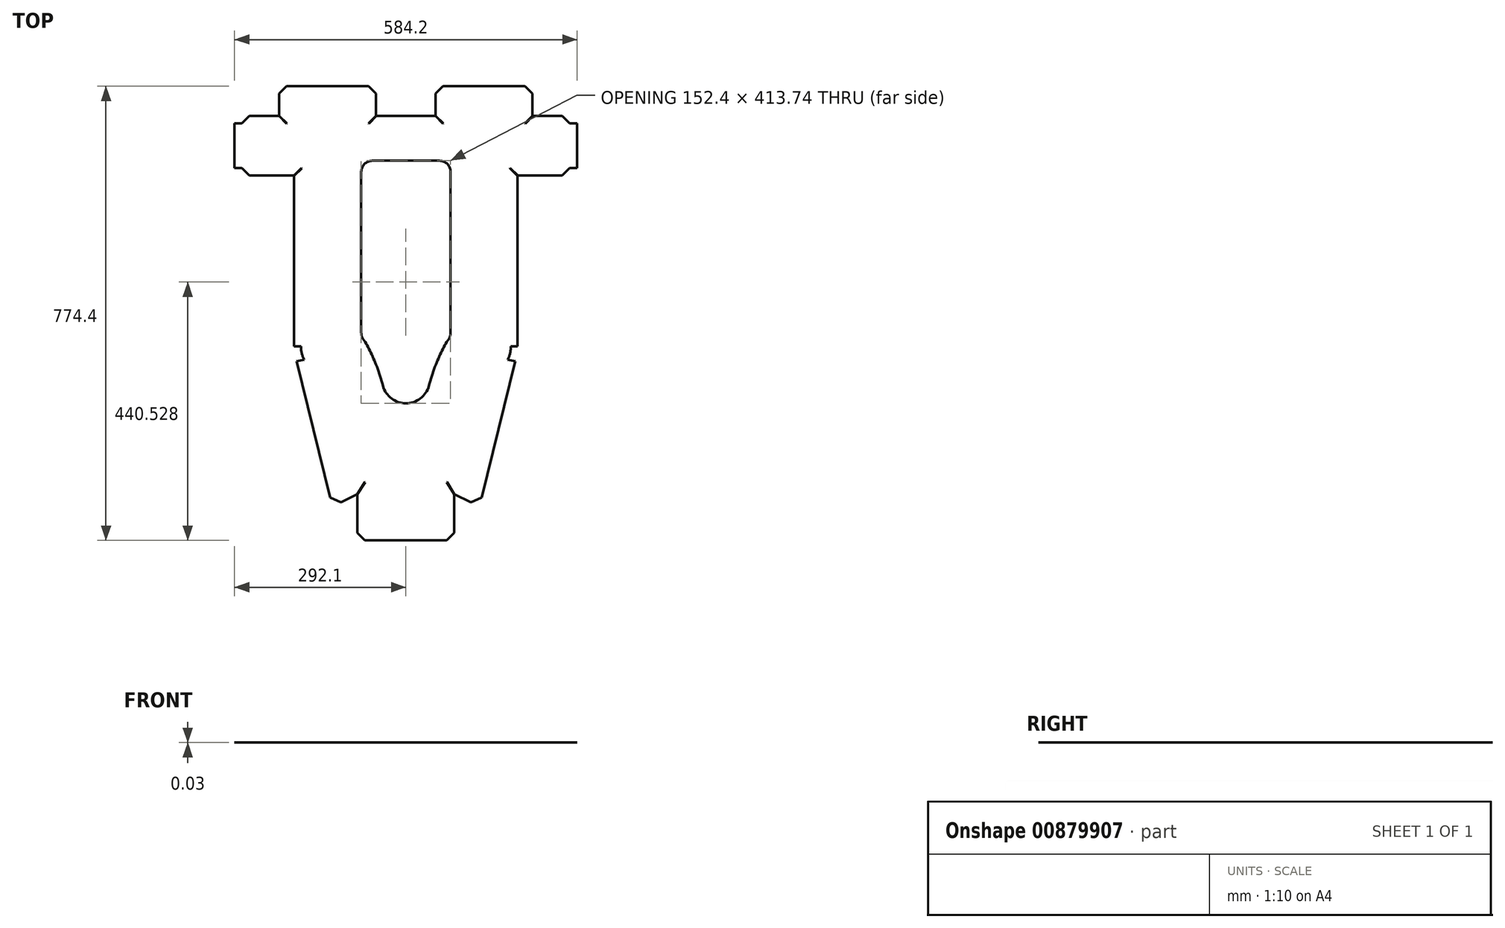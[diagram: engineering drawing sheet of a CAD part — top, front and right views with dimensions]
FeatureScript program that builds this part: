
annotation { "Feature Type Name" : "Feature", "Feature Type Description" : "" }
export const myFeature = defineFeature(function(context is Context, id is Id, definition is map)
    precondition{}
    {
        {
            var Q0;
            Q0=qCreatedBy(makeId("Top.planeOp"),FACE);
            var sketch = newSketch(context, id + "F0", { "sketchPlane" : qUnion([Q0])});
            skLineSegment(sketch, "E0", {"start": v(-107.95, 650.14) * mm, "end": v(-95.25, 650.14) * mm, "construction": true});
            skLineSegment(sketch, "E1", {"start": v(-76.2, 631.09) * mm, "end": v(-76.2, 599.34) * mm, "construction": true});
            skLineSegment(sketch, "E2", {"start": v(-76.2, 599.34) * mm, "end": v(0, 599.34) * mm, "construction": true});
            skLineSegment(sketch, "E3", {"start": v(-127, 631.09) * mm, "end": v(-127, 245.3) * mm, "construction": true});
            skPoint(sketch, "E4", {"position": v(-127, 232) * mm});
            skLineSegment(sketch, "E5", {"start": v(0, 599.34) * mm, "end": v(0, 0) * mm, "construction": true});
            skLineSegment(sketch, "E6", {"start": v(0, 0) * mm, "end": v(-69.85, 0) * mm, "construction": true});
            skLineSegment(sketch, "E7", {"start": v(-69.85, 0) * mm, "end": v(-69.85, -22.66) * mm, "construction": true});
            skLineSegment(sketch, "E8", {"start": v(-69.85, -22.66) * mm, "end": v(0, -22.66) * mm, "construction": true});
            skPoint(sketch, "E9.visualSharp", {"position": v(-127, 650.14) * mm});
            skArc(sketch, "E9.filletArc", {"start": v(-107.95, 650.14) * mm, "mid": v(-121.42, 644.56) * mm, "end": v(-127, 631.09) * mm, "construction": true});
            skPoint(sketch, "E10.visualSharp", {"position": v(-76.2, 650.14) * mm});
            skArc(sketch, "E10.filletArc", {"start": v(-76.2, 631.09) * mm, "mid": v(-81.78, 644.56) * mm, "end": v(-95.25, 650.14) * mm, "construction": true});
            skLineSegment(sketch, "E11", {"start": v(-190.5, 523.14) * mm, "end": v(-190.5, 232) * mm});
            skLineSegment(sketch, "E12", {"start": v(0, 624.74) * mm, "end": v(-50.8, 624.74) * mm});
            skLineSegment(sketch, "E13", {"start": v(-127, 232) * mm, "end": v(-69.85, 0) * mm, "construction": true});
            skLineSegment(sketch, "E14", {"start": v(-127, 232) * mm, "end": v(-185.44, 203.74) * mm, "construction": true});
            skLineSegment(sketch, "E15", {"start": v(-185.44, 203.74) * mm, "end": v(-128.93, -25.64) * mm});
            skLineSegment(sketch, "E16", {"start": v(-127, 232) * mm, "end": v(0, 232) * mm, "construction": true});
            skLineSegment(sketch, "E17", {"start": v(-127, 232) * mm, "end": v(-190.5, 232) * mm, "construction": true});
            skPoint(sketch, "E18.endSnap0", {"position": v(-177.62, 220.4) * mm});
            skLineSegment(sketch, "E19", {"start": v(-177.62, 220.4) * mm, "end": v(-127, 232) * mm, "construction": true});
            skLineSegment(sketch, "E20", {"start": v(-82.55, -86.16) * mm, "end": v(-82.55, -20.25) * mm});
            skLineSegment(sketch, "E21", {"start": v(-82.55, -20.25) * mm, "end": v(-69.85, 0) * mm, "construction": true});
            skLineSegment(sketch, "E22", {"start": v(-82.55, -86.16) * mm, "end": v(-69.85, -86.16) * mm, "construction": true});
            skLineSegment(sketch, "E23", {"start": v(-69.85, -86.16) * mm, "end": v(-69.85, -98.86) * mm, "construction": true});
            skLineSegment(sketch, "E24", {"start": v(-69.85, -98.86) * mm, "end": v(0, -98.86) * mm});
            skLineSegment(sketch, "E25", {"start": v(-111.07, -34.04) * mm, "end": v(-82.55, -20.25) * mm});
            skLineSegment(sketch, "E26", {"start": v(-69.85, -98.86) * mm, "end": v(-82.55, -86.16) * mm});
            skPoint(sketch, "E27.orphan", {"position": v(-127, 599.34) * mm});
            skLineSegment(sketch, "E28.MirrorCS", {"start": v(190.5, 523.14) * mm, "end": v(190.5, 232) * mm});
            skLineSegment(sketch, "E29.MirrorCS", {"start": v(185.44, 203.74) * mm, "end": v(128.93, -25.64) * mm});
            skLineSegment(sketch, "E30.MirrorCS", {"start": v(111.07, -34.04) * mm, "end": v(82.55, -20.25) * mm});
            skLineSegment(sketch, "E31.MirrorCS", {"start": v(82.55, -86.16) * mm, "end": v(82.55, -20.25) * mm});
            skLineSegment(sketch, "E32.MirrorCS", {"start": v(69.85, -98.86) * mm, "end": v(82.55, -86.16) * mm});
            skLineSegment(sketch, "E33.MirrorCS", {"start": v(69.85, -98.86) * mm, "end": v(0, -98.86) * mm});
            skLineSegment(sketch, "E34.MirrorCS", {"start": v(82.55, -20.25) * mm, "end": v(69.85, 0) * mm, "construction": true});
            skArc(sketch, "E35", {"start": v(-178.93, 232) * mm, "mid": v(-177.62, 220.4) * mm, "end": v(-173.75, 209.4) * mm});
            skLineSegment(sketch, "E36", {"start": v(-178.93, 232) * mm, "end": v(-190.5, 232) * mm});
            skLineSegment(sketch, "E37", {"start": v(-173.75, 209.4) * mm, "end": v(-186.08, 206.36) * mm});
            skLineSegment(sketch, "E38", {"start": v(-186.08, 206.36) * mm, "end": v(-185.44, 203.74) * mm});
            skArc(sketch, "E39.MirrorCS", {"start": v(178.93, 232) * mm, "mid": v(177.62, 220.4) * mm, "end": v(173.75, 209.4) * mm});
            skLineSegment(sketch, "E40.MirrorCS", {"start": v(178.93, 232) * mm, "end": v(190.5, 232) * mm});
            skLineSegment(sketch, "E41", {"start": v(-128.93, -25.64) * mm, "end": v(-116.6, -22.6) * mm, "construction": true});
            skLineSegment(sketch, "E42", {"start": v(-116.6, -22.6) * mm, "end": v(-111.07, -34.04) * mm, "construction": true});
            skLineSegment(sketch, "E43", {"start": v(-69.85, 0) * mm, "end": v(-116.6, -22.6) * mm, "construction": true});
            skLineSegment(sketch, "E44.MirrorCS", {"start": v(173.75, 209.4) * mm, "end": v(186.08, 206.36) * mm});
            skLineSegment(sketch, "E45.MirrorCS", {"start": v(186.08, 206.36) * mm, "end": v(185.44, 203.74) * mm});
            skLineSegment(sketch, "E46", {"start": v(-128.93, -25.64) * mm, "end": v(-111.07, -34.04) * mm});
            skLineSegment(sketch, "E47.MirrorCS", {"start": v(128.93, -25.64) * mm, "end": v(111.07, -34.04) * mm});
            skLineSegment(sketch, "E48", {"start": v(-190.5, 523.14) * mm, "end": v(-177.8, 535.84) * mm, "construction": true});
            skLineSegment(sketch, "E49", {"start": v(-190.5, 523.14) * mm, "end": v(-266.7, 523.14) * mm});
            skLineSegment(sketch, "E50", {"start": v(-266.7, 523.14) * mm, "end": v(-266.7, 535.84) * mm, "construction": true});
            skLineSegment(sketch, "E51", {"start": v(-279.4, 535.84) * mm, "end": v(-292.1, 535.84) * mm});
            skLineSegment(sketch, "E52", {"start": v(-292.1, 535.84) * mm, "end": v(-292.1, 612.04) * mm});
            skLineSegment(sketch, "E53", {"start": v(-50.8, 624.74) * mm, "end": v(-50.8, 662.84) * mm});
            skLineSegment(sketch, "E54", {"start": v(-50.8, 624.74) * mm, "end": v(-63.5, 612.04) * mm, "construction": true});
            skLineSegment(sketch, "E55", {"start": v(-63.5, 612.04) * mm, "end": v(-76.2, 612.04) * mm, "construction": true});
            skLineSegment(sketch, "E56", {"start": v(-63.5, 612.04) * mm, "end": v(-63.5, 599.34) * mm, "construction": true});
            skLineSegment(sketch, "E57", {"start": v(-292.1, 612.04) * mm, "end": v(-279.4, 612.04) * mm});
            skLineSegment(sketch, "E58", {"start": v(-266.7, 612.04) * mm, "end": v(-266.7, 624.74) * mm, "construction": true});
            skLineSegment(sketch, "E59", {"start": v(-127, 675.54) * mm, "end": v(-63.5, 675.54) * mm});
            skPoint(sketch, "E60", {"position": v(-63.5, 662.84) * mm});
            skLineSegment(sketch, "E61", {"start": v(-279.4, 535.84) * mm, "end": v(-266.7, 523.14) * mm});
            skLineSegment(sketch, "E62", {"start": v(-279.4, 612.04) * mm, "end": v(-266.7, 624.74) * mm});
            skLineSegment(sketch, "E63", {"start": v(-266.7, 612.04) * mm, "end": v(-279.4, 612.04) * mm, "construction": true});
            skLineSegment(sketch, "E64", {"start": v(-279.4, 535.84) * mm, "end": v(-266.7, 535.84) * mm, "construction": true});
            skLineSegment(sketch, "E65", {"start": v(-127, 675.54) * mm, "end": v(-203.2, 675.54) * mm});
            skLineSegment(sketch, "E66", {"start": v(-215.9, 662.84) * mm, "end": v(-215.9, 624.74) * mm});
            skLineSegment(sketch, "E67", {"start": v(-266.7, 624.74) * mm, "end": v(-215.9, 624.74) * mm});
            skLineSegment(sketch, "E68", {"start": v(-215.9, 624.74) * mm, "end": v(-203.2, 612.04) * mm, "construction": true});
            skLineSegment(sketch, "E69.MirrorCS", {"start": v(190.5, 523.14) * mm, "end": v(177.8, 535.84) * mm, "construction": true});
            skLineSegment(sketch, "E70.MirrorCS", {"start": v(190.5, 523.14) * mm, "end": v(266.7, 523.14) * mm});
            skLineSegment(sketch, "E71.MirrorCS", {"start": v(279.4, 535.84) * mm, "end": v(266.7, 523.14) * mm});
            skLineSegment(sketch, "E72.MirrorCS", {"start": v(279.4, 535.84) * mm, "end": v(292.1, 535.84) * mm});
            skLineSegment(sketch, "E73.MirrorCS", {"start": v(292.1, 535.84) * mm, "end": v(292.1, 612.04) * mm});
            skLineSegment(sketch, "E74.MirrorCS", {"start": v(292.1, 612.04) * mm, "end": v(279.4, 612.04) * mm});
            skLineSegment(sketch, "E75.MirrorCS", {"start": v(279.4, 612.04) * mm, "end": v(266.7, 624.74) * mm});
            skLineSegment(sketch, "E76.MirrorCS", {"start": v(266.7, 624.74) * mm, "end": v(215.9, 624.74) * mm});
            skLineSegment(sketch, "E77.MirrorCS", {"start": v(215.9, 624.74) * mm, "end": v(203.2, 612.04) * mm, "construction": true});
            skLineSegment(sketch, "E78.MirrorCS", {"start": v(50.8, 624.74) * mm, "end": v(63.5, 612.04) * mm, "construction": true});
            skLineSegment(sketch, "E79.MirrorCS", {"start": v(0, 624.74) * mm, "end": v(50.8, 624.74) * mm});
            skLineSegment(sketch, "E80", {"start": v(-215.9, 662.84) * mm, "end": v(-203.2, 675.54) * mm});
            skPoint(sketch, "E81", {"position": v(-63.5, 675.54) * mm});
            skPoint(sketch, "E82", {"position": v(-50.8, 662.84) * mm});
            skLineSegment(sketch, "E83", {"start": v(-63.5, 675.54) * mm, "end": v(-50.8, 662.84) * mm});
            skLineSegment(sketch, "E84.MirrorCS", {"start": v(215.9, 662.84) * mm, "end": v(215.9, 624.74) * mm});
            skLineSegment(sketch, "E85.MirrorCS", {"start": v(215.9, 662.84) * mm, "end": v(203.2, 675.54) * mm});
            skLineSegment(sketch, "E86.MirrorCS", {"start": v(127, 675.54) * mm, "end": v(203.2, 675.54) * mm});
            skLineSegment(sketch, "E87.MirrorCS", {"start": v(127, 675.54) * mm, "end": v(63.5, 675.54) * mm});
            skLineSegment(sketch, "E88.MirrorCS", {"start": v(63.5, 675.54) * mm, "end": v(50.8, 662.84) * mm});
            skLineSegment(sketch, "E89.MirrorCS", {"start": v(50.8, 624.74) * mm, "end": v(50.8, 662.84) * mm});
            skLineSegment(sketch, "E90", {"start": v(0, 548.54) * mm, "end": v(-57.15, 548.54) * mm, "construction": true});
            skPoint(sketch, "E91", {"position": v(0, 134.8) * mm});
            skArc(sketch, "E92", {"start": v(0, 134.8) * mm, "mid": v(-24.7, 143.14) * mm, "end": v(-39.26, 164.76) * mm});
            skArc(sketch, "E93", {"start": v(0, 548.54) * mm, "mid": v(-53.88, 526.22) * mm, "end": v(-76.2, 472.34) * mm, "construction": true});
            skLineSegment(sketch, "E94", {"start": v(-76.2, 472.34) * mm, "end": v(-76.2, 255.45) * mm});
            skLineSegment(sketch, "E95", {"start": v(-76.2, 529.49) * mm, "end": v(-76.2, 472.34) * mm});
            skPoint(sketch, "E96.visualSharp", {"position": v(-76.2, 548.54) * mm});
            skArc(sketch, "E97", {"start": v(-73.04, 244.94) * mm, "mid": v(-75.4, 249.96) * mm, "end": v(-76.2, 255.45) * mm});
            skLineSegment(sketch, "E98", {"start": v(0, 548.54) * mm, "end": v(-57.15, 548.54) * mm});
            skArc(sketch, "E99.MirrorCS", {"start": v(73.04, 244.94) * mm, "mid": v(75.4, 249.96) * mm, "end": v(76.2, 255.45) * mm});
            skArc(sketch, "E100", {"start": v(-76.2, 529.49) * mm, "mid": v(-70.62, 542.96) * mm, "end": v(-57.15, 548.54) * mm});
            skArc(sketch, "E101", {"start": v(0, 548.54) * mm, "mid": v(53.88, 526.22) * mm, "end": v(76.2, 472.34) * mm, "construction": true});
            skLineSegment(sketch, "E102", {"start": v(76.2, 472.34) * mm, "end": v(76.2, 255.45) * mm});
            skLineSegment(sketch, "E103.MirrorCS", {"start": v(0, 548.54) * mm, "end": v(57.15, 548.54) * mm});
            skArc(sketch, "E104.MirrorCS", {"start": v(76.2, 529.49) * mm, "mid": v(70.62, 542.96) * mm, "end": v(57.15, 548.54) * mm});
            skLineSegment(sketch, "E105.MirrorCS", {"start": v(76.2, 529.49) * mm, "end": v(76.2, 472.34) * mm});
            skLineSegment(sketch, "E106.MirrorCS", {"start": v(76.2, 599.34) * mm, "end": v(0, 599.34) * mm, "construction": true});
            skLineSegment(sketch, "E107.MirrorCS", {"start": v(76.2, 631.09) * mm, "end": v(76.2, 599.34) * mm, "construction": true});
            skArc(sketch, "E108.MirrorCS", {"start": v(76.2, 631.09) * mm, "mid": v(81.78, 644.56) * mm, "end": v(95.25, 650.14) * mm, "construction": true});
            skLineSegment(sketch, "E109.MirrorCS", {"start": v(107.95, 650.14) * mm, "end": v(95.25, 650.14) * mm, "construction": true});
            skArc(sketch, "E110.MirrorCS", {"start": v(107.95, 650.14) * mm, "mid": v(121.42, 644.56) * mm, "end": v(127, 631.09) * mm, "construction": true});
            skLineSegment(sketch, "E111.MirrorCS", {"start": v(127, 631.09) * mm, "end": v(127, 245.3) * mm, "construction": true});
            skLineSegment(sketch, "E112", {"start": v(-57.15, 548.54) * mm, "end": v(-76.2, 548.54) * mm, "construction": true});
            skLineSegment(sketch, "E113", {"start": v(57.15, 548.54) * mm, "end": v(76.2, 548.54) * mm, "construction": true});
            skEllipse(sketch, "E114", {"center": v(-127, 0) * mm, "majorRadius": 232 * mm, "minorRadius": 57.15 * mm, "majorAxis": v(0, 1), "construction": true});
            skArc(sketch, "E115", {"start": v(-127, 245.3) * mm, "mid": v(-124.65, 236.12) * mm, "end": v(-118.16, 229.21) * mm, "construction": true});
            skPoint(sketch, "E116", {"position": v(-127, 282.8) * mm});
            skPoint(sketch, "E117", {"position": v(-19.05, 0) * mm});
            skEllipse(sketch, "E118.MirrorC", {"center": v(127, 0) * mm, "majorRadius": 232 * mm, "minorRadius": 57.15 * mm, "majorAxis": v(0, 1), "construction": true});
            skArc(sketch, "E119.MirrorCS", {"start": v(127, 245.3) * mm, "mid": v(124.65, 236.12) * mm, "end": v(118.16, 229.21) * mm, "construction": true});
            skEllipticalArc(sketch, "E120", {});
            skEllipticalArc(sketch, "E121", {"construction": true});
            skArc(sketch, "E122.MirrorCS", {"start": v(0, 134.8) * mm, "mid": v(24.7, 143.14) * mm, "end": v(39.26, 164.76) * mm});
            skEllipticalArc(sketch, "E123.MirrorCS", {});
            const initialGuessF0  = {"E120": [-0.127, 0, 0, 1, 0.28280360000000004, 0.10795, 5.33430943767828, 5.7597386580573735], "E121": [-0.127, 0, 0, 1, 0.28280360000000004, 0.10795, 5.7597386580573735, 5.33430943767828], "E123.MirrorCS": [0.127, 0, 0, 1, 0.28280360000000004, 0.10795, 0.5234466491222127, 0.9488758695013066]};
            skSetInitialGuess(sketch, initialGuessF0);
            skSolve(sketch);
        }
        {
            var Q0;
            Q0=qSketchRegion(id+"F0",true);
            extrude(context, id + "F1", {"entities" : qUnion([Q0]), "depth" : 0.03 * mm, "offsetDistance" : 25.4 * mm});
        }
        {
            var Q0;
            Q0=qCreatedBy(makeId("Top.planeOp"),FACE);
            var sketch = newSketch(context, id + "F2", { "sketchPlane" : qUnion([Q0])});
            skLineSegment(sketch, "E124", {"start": v(-215.9, 624.76) * mm, "end": v(-203.2, 612.05) * mm});
            skLineSegment(sketch, "E125", {"start": v(-203.2, 612.05) * mm, "end": v(-203.2, 612.03) * mm});
            skLineSegment(sketch, "E126", {"start": v(-203.2, 612.03) * mm, "end": v(-215.92, 624.74) * mm});
            skLineSegment(sketch, "E127", {"start": v(-215.9, 624.76) * mm, "end": v(-215.92, 624.74) * mm});
            skLineSegment(sketch, "E128", {"start": v(-50.8, 624.76) * mm, "end": v(-63.5, 612.05) * mm});
            skLineSegment(sketch, "E129", {"start": v(-63.5, 612.05) * mm, "end": v(-63.5, 612.03) * mm});
            skLineSegment(sketch, "E130", {"start": v(-63.5, 612.03) * mm, "end": v(-50.78, 624.74) * mm});
            skLineSegment(sketch, "E131", {"start": v(0, 624.74) * mm, "end": v(0, -98.86) * mm, "construction": true});
            skLineSegment(sketch, "E132", {"start": v(-82.56, -20.24) * mm, "end": v(-69.86, 0) * mm});
            skLineSegment(sketch, "E133", {"start": v(-69.86, 0) * mm, "end": v(-69.84, 0) * mm});
            skLineSegment(sketch, "E134", {"start": v(-69.84, 0) * mm, "end": v(-82.54, -20.26) * mm});
            skLineSegment(sketch, "E135", {"start": v(-82.54, -20.26) * mm, "end": v(-82.56, -20.24) * mm, "construction": true});
            skPoint(sketch, "E136", {"position": v(-82.55, -20.25) * mm});
            skPoint(sketch, "E137", {"position": v(-69.85, 0) * mm});
            skLineSegment(sketch, "E138.MirrorCS", {"start": v(50.78, 624.74) * mm, "end": v(50.8, 624.76) * mm});
            skLineSegment(sketch, "E139.MirrorCS", {"start": v(63.5, 612.03) * mm, "end": v(50.78, 624.74) * mm});
            skLineSegment(sketch, "E140.MirrorCS", {"start": v(63.5, 612.05) * mm, "end": v(63.5, 612.03) * mm});
            skLineSegment(sketch, "E141.MirrorCS", {"start": v(50.8, 624.76) * mm, "end": v(63.5, 612.05) * mm});
            skLineSegment(sketch, "E142.MirrorCS", {"start": v(203.2, 612.05) * mm, "end": v(203.2, 612.03) * mm});
            skLineSegment(sketch, "E143.MirrorCS", {"start": v(215.9, 624.76) * mm, "end": v(215.92, 624.74) * mm});
            skLineSegment(sketch, "E144.MirrorCS", {"start": v(203.2, 612.03) * mm, "end": v(215.92, 624.74) * mm});
            skLineSegment(sketch, "E145.MirrorCS", {"start": v(215.9, 624.76) * mm, "end": v(203.2, 612.05) * mm});
            skLineSegment(sketch, "E146.MirrorCS", {"start": v(82.54, -20.26) * mm, "end": v(82.56, -20.24) * mm, "construction": true});
            skLineSegment(sketch, "E147.MirrorCS", {"start": v(69.86, 0) * mm, "end": v(69.84, 0) * mm});
            skLineSegment(sketch, "E148.MirrorCS", {"start": v(69.84, 0) * mm, "end": v(82.54, -20.26) * mm});
            skPoint(sketch, "E149.MirrorP", {"position": v(82.55, -20.25) * mm});
            skPoint(sketch, "E150.MirrorP", {"position": v(69.85, 0) * mm});
            skLineSegment(sketch, "E151.MirrorCS", {"start": v(82.56, -20.24) * mm, "end": v(69.86, 0) * mm});
            skLineSegment(sketch, "E152", {"start": v(-50.8, 624.76) * mm, "end": v(-50.78, 624.74) * mm});
            skLineSegment(sketch, "E153.MirrorCS", {"start": v(50.8, 624.76) * mm, "end": v(50.78, 624.74) * mm});
            skLineSegment(sketch, "E154", {"start": v(-82.56, -20.24) * mm, "end": v(-82.57, -20.26) * mm});
            skLineSegment(sketch, "E155", {"start": v(-82.54, -20.26) * mm, "end": v(-82.55, -20.27) * mm});
            skLineSegment(sketch, "E156", {"start": v(-82.57, -20.26) * mm, "end": v(-82.55, -20.27) * mm});
            skLineSegment(sketch, "E157.MirrorCS", {"start": v(82.54, -20.26) * mm, "end": v(82.55, -20.27) * mm});
            skLineSegment(sketch, "E158.MirrorCS", {"start": v(82.56, -20.24) * mm, "end": v(82.57, -20.26) * mm});
            skLineSegment(sketch, "E159.MirrorCS", {"start": v(82.57, -20.26) * mm, "end": v(82.55, -20.27) * mm});
            skLineSegment(sketch, "E160", {"start": v(-190.52, 523.14) * mm, "end": v(-190.5, 523.12) * mm});
            skLineSegment(sketch, "E161", {"start": v(-190.5, 523.12) * mm, "end": v(-177.8, 535.83) * mm});
            skLineSegment(sketch, "E162", {"start": v(-177.8, 535.83) * mm, "end": v(-177.8, 535.85) * mm});
            skLineSegment(sketch, "E163", {"start": v(-177.8, 535.85) * mm, "end": v(-190.52, 523.14) * mm});
            skLineSegment(sketch, "E164.MirrorCS", {"start": v(190.52, 523.14) * mm, "end": v(190.5, 523.12) * mm});
            skLineSegment(sketch, "E165.MirrorCS", {"start": v(177.8, 535.85) * mm, "end": v(190.52, 523.14) * mm});
            skLineSegment(sketch, "E166.MirrorCS", {"start": v(177.8, 535.83) * mm, "end": v(177.8, 535.85) * mm});
            skLineSegment(sketch, "E167.MirrorCS", {"start": v(190.5, 523.12) * mm, "end": v(177.8, 535.83) * mm});
            skSolve(sketch);
        }
        {
            var Q0;
            Q0=qSketchRegion(id+"F2",true);
            extrude(context, id + "F3", {"entities" : qUnion([Q0]), "operationType" : NewBodyOperationType.REMOVE, "endBound" : BoundingType.THROUGH_ALL, "depth" : 25.4 * mm, "offsetDistance" : 25.4 * mm});
        }
    });
